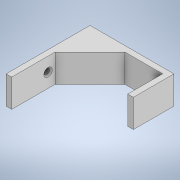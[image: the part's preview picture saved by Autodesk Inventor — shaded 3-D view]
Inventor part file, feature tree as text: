
AUTODESK INVENTOR PART (.ipt)
format: ipt  version: 2021.1 (Build 251245010, 245A)  size: 125,952 bytes
history: native  units: mm
features: extrude x3, sketch x3, other x1, chamfer x1
ambient origin geometry x8: Origin, YZ Plane, XZ Plane, XY Plane, X Axis, Y Axis, Z Axis, Center Point
bodies: Body1 (feature_tree)
feature tree (8):
  other  "Твердое тело1"
  extrude  "Выдавливание1"  Depth=4.0mm
  extrude  "Выдавливание2"  Depth=60.0mm
  chamfer  "Фаска1"  Distance=60.0mm
  extrude  "Выдавливание3"  Depth=4.0mm
  sketch  "Эскиз1"
  sketch  "Эскиз2"
  sketch  "Эскиз3"
